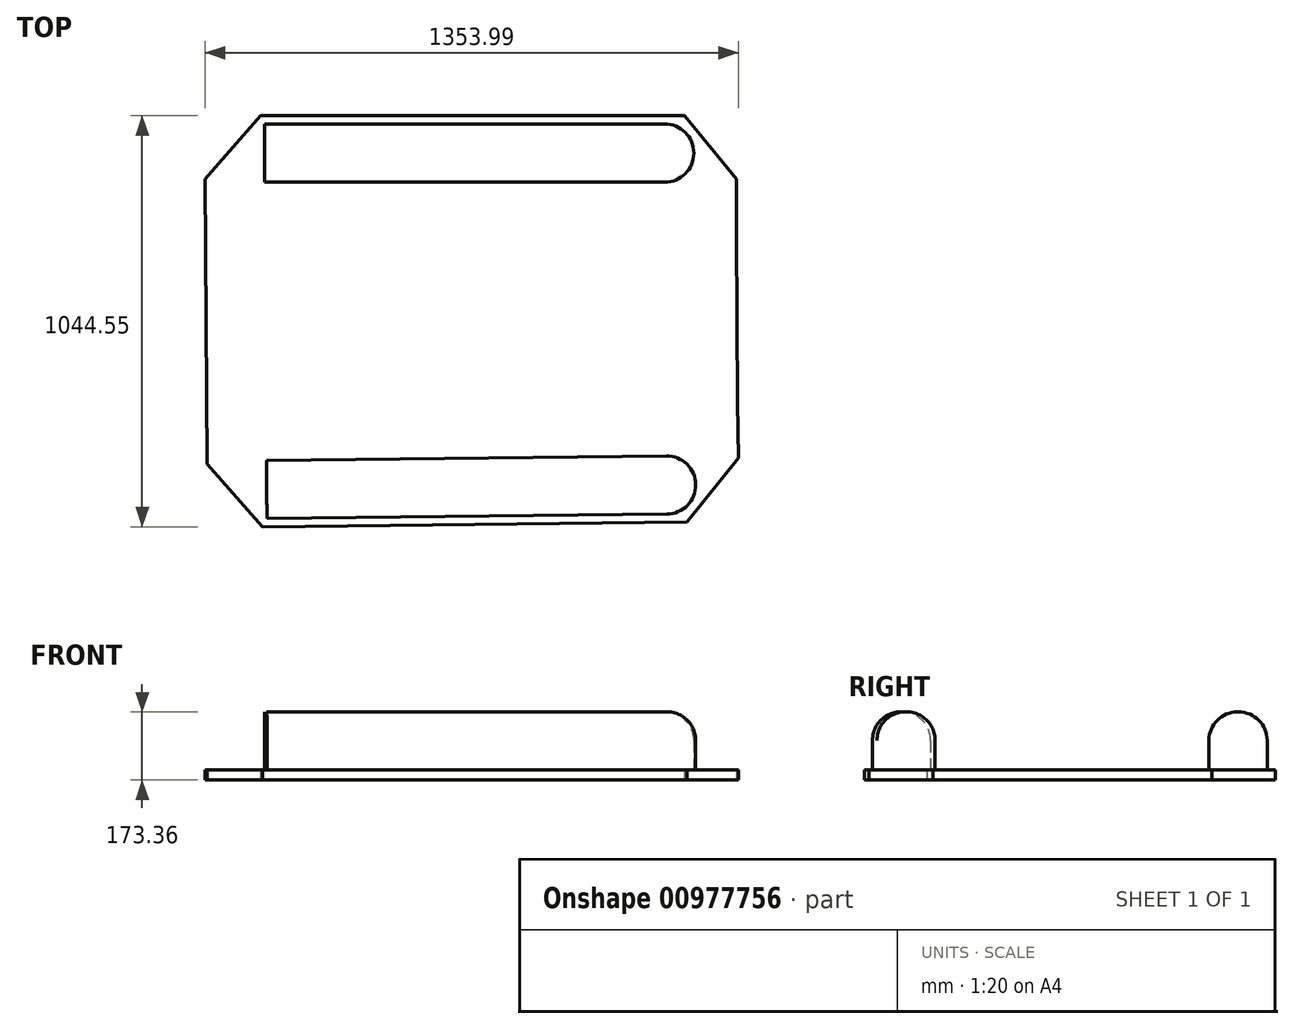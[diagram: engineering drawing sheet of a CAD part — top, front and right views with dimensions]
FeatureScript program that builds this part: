
annotation { "Feature Type Name" : "Feature", "Feature Type Description" : "" }
export const myFeature = defineFeature(function(context is Context, id is Id, definition is map)
    precondition{}
    {
        {
            var Q0;
            Q0=qCreatedBy(makeId("Top.planeOp"),FACE);
            var sketch = newSketch(context, id + "F0", { "sketchPlane" : qUnion([Q0])});
            skLineSegment(sketch, "E0.bottom", {"start": v(1828.8, 457.2) * mm, "end": v(-1828.8, 457.2) * mm});
            skLineSegment(sketch, "E0.top", {"start": v(1828.8, -457.2) * mm, "end": v(-1828.8, -457.2) * mm});
            skLineSegment(sketch, "E0.left", {"start": v(1828.8, 457.2) * mm, "end": v(1828.8, -457.2) * mm});
            skLineSegment(sketch, "E0.right", {"start": v(-1828.8, 457.2) * mm, "end": v(-1828.8, -457.2) * mm});
            skPoint(sketch, "E0.middle", {"position": v(0, 0) * mm});
            skSolve(sketch);
        }
        {
            var Q0;
            Q0=makeQuery(id+"F0.imprint","IMPRINT",FACE,{"disambiguationData":[TD([[makeQuery(id+"F0.imprint","IMPRINT",EDGE,{"derivedFrom":sQuery(id+"F0.wireOp",EDGE,"E0.bottom")}),1.0]])]});
            var sketch = newSketch(context, id + "F1", { "sketchPlane" : qUnion([Q0])});
            skLineSegment(sketch, "E1", {"start": v(-1564.43, -10.09) * mm, "end": v(1587.54, 7.59) * mm, "construction": true});
            skLineSegment(sketch, "E2", {"start": v(236.33, 362.08) * mm, "end": v(240.4, -362.03) * mm});
            skLineSegment(sketch, "E3", {"start": v(240.4, -362.03) * mm, "end": v(382.18, -521.46) * mm});
            skLineSegment(sketch, "E4", {"start": v(1587.54, 7.59) * mm, "end": v(1588.73, -205.77) * mm});
            skLineSegment(sketch, "E5.MirrorCS", {"start": v(236.33, 362.08) * mm, "end": v(376.32, 523.09) * mm});
            skLineSegment(sketch, "E6.MirrorCS", {"start": v(1587.54, 7.59) * mm, "end": v(1586.34, 220.95) * mm});
            skPoint(sketch, "E7.10.internal.orphan", {"position": v(592.77, 2.01) * mm});
            skPoint(sketch, "E7.start.orphan", {"position": v(-502.96, -4.13) * mm});
            skPoint(sketch, "E8.13.internal.orphan", {"position": v(639.1, 2.27) * mm});
            skPoint(sketch, "E8.start.orphan", {"position": v(-552.56, -4.41) * mm});
            skPoint(sketch, "E9.13.internal.orphan", {"position": v(729.84, 2.78) * mm});
            skPoint(sketch, "E9.start.orphan", {"position": v(-611.36, -4.74) * mm});
            skPoint(sketch, "E10.MirrorCS.27.internal.orphan", {"position": v(1587.54, 7.59) * mm});
            skPoint(sketch, "E10.MirrorCS.start.orphan", {"position": v(-1564.43, -10.09) * mm});
            skLineSegment(sketch, "E11", {"start": v(376.32, 523.09) * mm, "end": v(1453.8, 523.09) * mm});
            skLineSegment(sketch, "E12", {"start": v(1586.34, 220.95) * mm, "end": v(1586.34, 362.08) * mm});
            skPoint(sketch, "E13.MirrorCS.end.orphan", {"position": v(376.32, 523.09) * mm});
            skPoint(sketch, "E14.MirrorCS.end.orphan", {"position": v(1586.34, 523.09) * mm});
            skPoint(sketch, "E14.MirrorCS.start.orphan", {"position": v(1586.34, 825.23) * mm});
            skLineSegment(sketch, "E15", {"start": v(1586.34, 362.08) * mm, "end": v(1453.8, 523.09) * mm});
            skLineSegment(sketch, "E16.MirrorCS", {"start": v(382.18, -521.46) * mm, "end": v(1459.58, -509.38) * mm});
            skLineSegment(sketch, "E17.MirrorCS", {"start": v(1590.32, -346.9) * mm, "end": v(1459.58, -509.38) * mm});
            skLineSegment(sketch, "E18.MirrorCS", {"start": v(1588.73, -205.77) * mm, "end": v(1590.32, -346.9) * mm});
            skSolve(sketch);
        }
        {
            var Q0;
            {var subQ10=sQuery(id+"F1.wireOp",EDGE,"E2");Q0=makeQuery(id+"F1.imprint","IMPRINT",FACE,{"disambiguationData":[TD([[makeQuery(id+"F1.imprint","IMPRINT",EDGE,{"derivedFrom":subQ10}),1.0]])]});}
            var Q1;
            {var subQ0=sQuery(id+"F1.wireOp",EDGE,"1ON659qF-ZjNW-x03v-gTAe-3omuAMdhsX5g");var subQ1=sQuery(id+"F1.wireOp",EDGE,"E3");var subQ2=makeQuery(id+"F1.imprint","INTERSECT",VERTEX,{"derivedFrom":[subQ1,subQ0]});Q1=makeQuery(id+"F1.imprint","IMPRINT",FACE,{"disambiguationData":[TD([[makeQuery(id+"F1.imprint","IMPRINT",EDGE,{"disambiguationData":[TD([[subQ2,1.0]])],"derivedFrom":subQ1}),1.0]])]});}
            var Q2;
            {var subQ0=sQuery(id+"F1.wireOp",EDGE,"E13.MirrorCS");var subQ1=sQuery(id+"F1.wireOp",EDGE,"E5.MirrorCS");var subQ2=makeQuery(id+"F1.imprint","INTERSECT",VERTEX,{"derivedFrom":[subQ1,subQ0]});Q2=makeQuery(id+"F1.imprint","IMPRINT",FACE,{"disambiguationData":[TD([[makeQuery(id+"F1.imprint","IMPRINT",EDGE,{"disambiguationData":[TD([[subQ2,1.0]])],"derivedFrom":subQ1}),-1.0]])]});}
            extrude(context, id + "F2", {"entities" : qUnion([Q0, Q1, Q2]), "depth" : 25.4 * mm, "offsetDistance" : 25.4 * mm});
        }
        {
            var Q0;
            Q0=makeQuery(id+"F2.opExtrude","CAP_FACE",FACE,{"disambiguationData":[OSD([sQuery(id+"F1.wireOp",EDGE,"E2"),sQuery(id+"F1.wireOp",EDGE,"E3"),sQuery(id+"F1.wireOp",EDGE,"E5.MirrorCS"),sQuery(id+"F1.wireOp",EDGE,"E6.MirrorCS"),sQuery(id+"F1.wireOp",EDGE,"E11"),sQuery(id+"F1.wireOp",EDGE,"E12"),sQuery(id+"F1.wireOp",EDGE,"E15"),sQuery(id+"F1.wireOp",EDGE,"E16.MirrorCS"),sQuery(id+"F1.wireOp",EDGE,"E17.MirrorCS"),sQuery(id+"F1.wireOp",EDGE,"E4"),sQuery(id+"F1.wireOp",EDGE,"E18.MirrorCS")])],"isStart":false});
            var sketch = newSketch(context, id + "F3", { "sketchPlane" : qUnion([Q0])});
            skLineSegment(sketch, "E19", {"start": v(1587.54, 7.59) * mm, "end": v(238.36, 0) * mm, "construction": true});
            skLineSegment(sketch, "E20.bottom", {"start": v(387.47, 354.25) * mm, "end": v(1403.47, 354.25) * mm});
            skLineSegment(sketch, "E20.top", {"start": v(387.47, 502.2) * mm, "end": v(1403.47, 502.2) * mm});
            skLineSegment(sketch, "E20.left", {"start": v(387.47, 354.25) * mm, "end": v(387.47, 502.2) * mm});
            skLineSegment(sketch, "E20.right", {"start": v(1403.47, 354.25) * mm, "end": v(1403.47, 502.2) * mm});
            skArc(sketch, "E21", {"start": v(1403.47, 354.25) * mm, "mid": v(1477.45, 428.23) * mm, "end": v(1403.47, 502.2) * mm});
            skLineSegment(sketch, "E22.MirrorCS", {"start": v(393.12, -500.5) * mm, "end": v(1409.05, -489.07) * mm});
            skLineSegment(sketch, "E23.MirrorCS", {"start": v(391.45, -352.55) * mm, "end": v(1407.39, -341.12) * mm});
            skLineSegment(sketch, "E24.MirrorCS", {"start": v(391.45, -352.55) * mm, "end": v(393.12, -500.5) * mm});
            skArc(sketch, "E25.MirrorCS", {"start": v(1407.39, -341.12) * mm, "mid": v(1482.2, -414.26) * mm, "end": v(1409.05, -489.07) * mm});
            skLineSegment(sketch, "E26.MirrorCS", {"start": v(1407.39, -341.12) * mm, "end": v(1409.05, -489.07) * mm});
            skSolve(sketch);
        }
        {
            var Q0;
            Q0 = qSketchRegion(id + "F3", true);
            extrude(context, id + "F4", {"entities" : qUnion([Q0]), "operationType" : NewBodyOperationType.ADD, "depth" : 147.95 * mm, "offsetDistance" : 25.4 * mm});
        }
        {
            var Q0;
            Q0 = qSketchRegion(id + "F3", true);
            extrude(context, id + "F5", {"entities" : qUnion([Q0]), "operationType" : NewBodyOperationType.ADD, "depth" : 133.55 * mm, "offsetDistance" : 25.4 * mm});
        }
        {
            var Q0;
            Q0=makeQuery(id+"F4.opExtrude","CAP_EDGE",EDGE,{"disambiguationData":[OSD([sQuery(id+"F3.wireOp",EDGE,"E20.top")])],"isStart":false});
            var Q1;
            Q1=makeQuery(id+"F4.opExtrude","CAP_EDGE",EDGE,{"disambiguationData":[OSD([sQuery(id+"F3.wireOp",EDGE,"E21")])],"isStart":false});
            var Q2;
            Q2=makeQuery(id+"F4.opExtrude","CAP_EDGE",EDGE,{"disambiguationData":[OSD([sQuery(id+"F3.wireOp",EDGE,"E20.bottom")])],"isStart":false});
            fillet(context, id + "F6", {"entities" : qUnion([Q0, Q1, Q2]), "radius" : 72.39 * mm, "tangentPropagation" : true, "allowEdgeOverflow" : false});
        }
        {
            var Q0;
            Q0=makeQuery(id+"F4.opExtrude","CAP_EDGE",EDGE,{"disambiguationData":[OSD([sQuery(id+"F3.wireOp",EDGE,"E23.MirrorCS")])],"isStart":false});
            var Q1;
            Q1=makeQuery(id+"F4.opExtrude","CAP_EDGE",EDGE,{"disambiguationData":[OSD([sQuery(id+"F3.wireOp",EDGE,"E25.MirrorCS")])],"isStart":false});
            var Q2;
            Q2=makeQuery(id+"F4.opExtrude","CAP_EDGE",EDGE,{"disambiguationData":[OSD([sQuery(id+"F3.wireOp",EDGE,"E22.MirrorCS")])],"isStart":false});
            fillet(context, id + "F7", {"entities" : qUnion([Q0, Q1, Q2]), "radius" : 72.39 * mm, "tangentPropagation" : true, "allowEdgeOverflow" : false});
        }
    });
